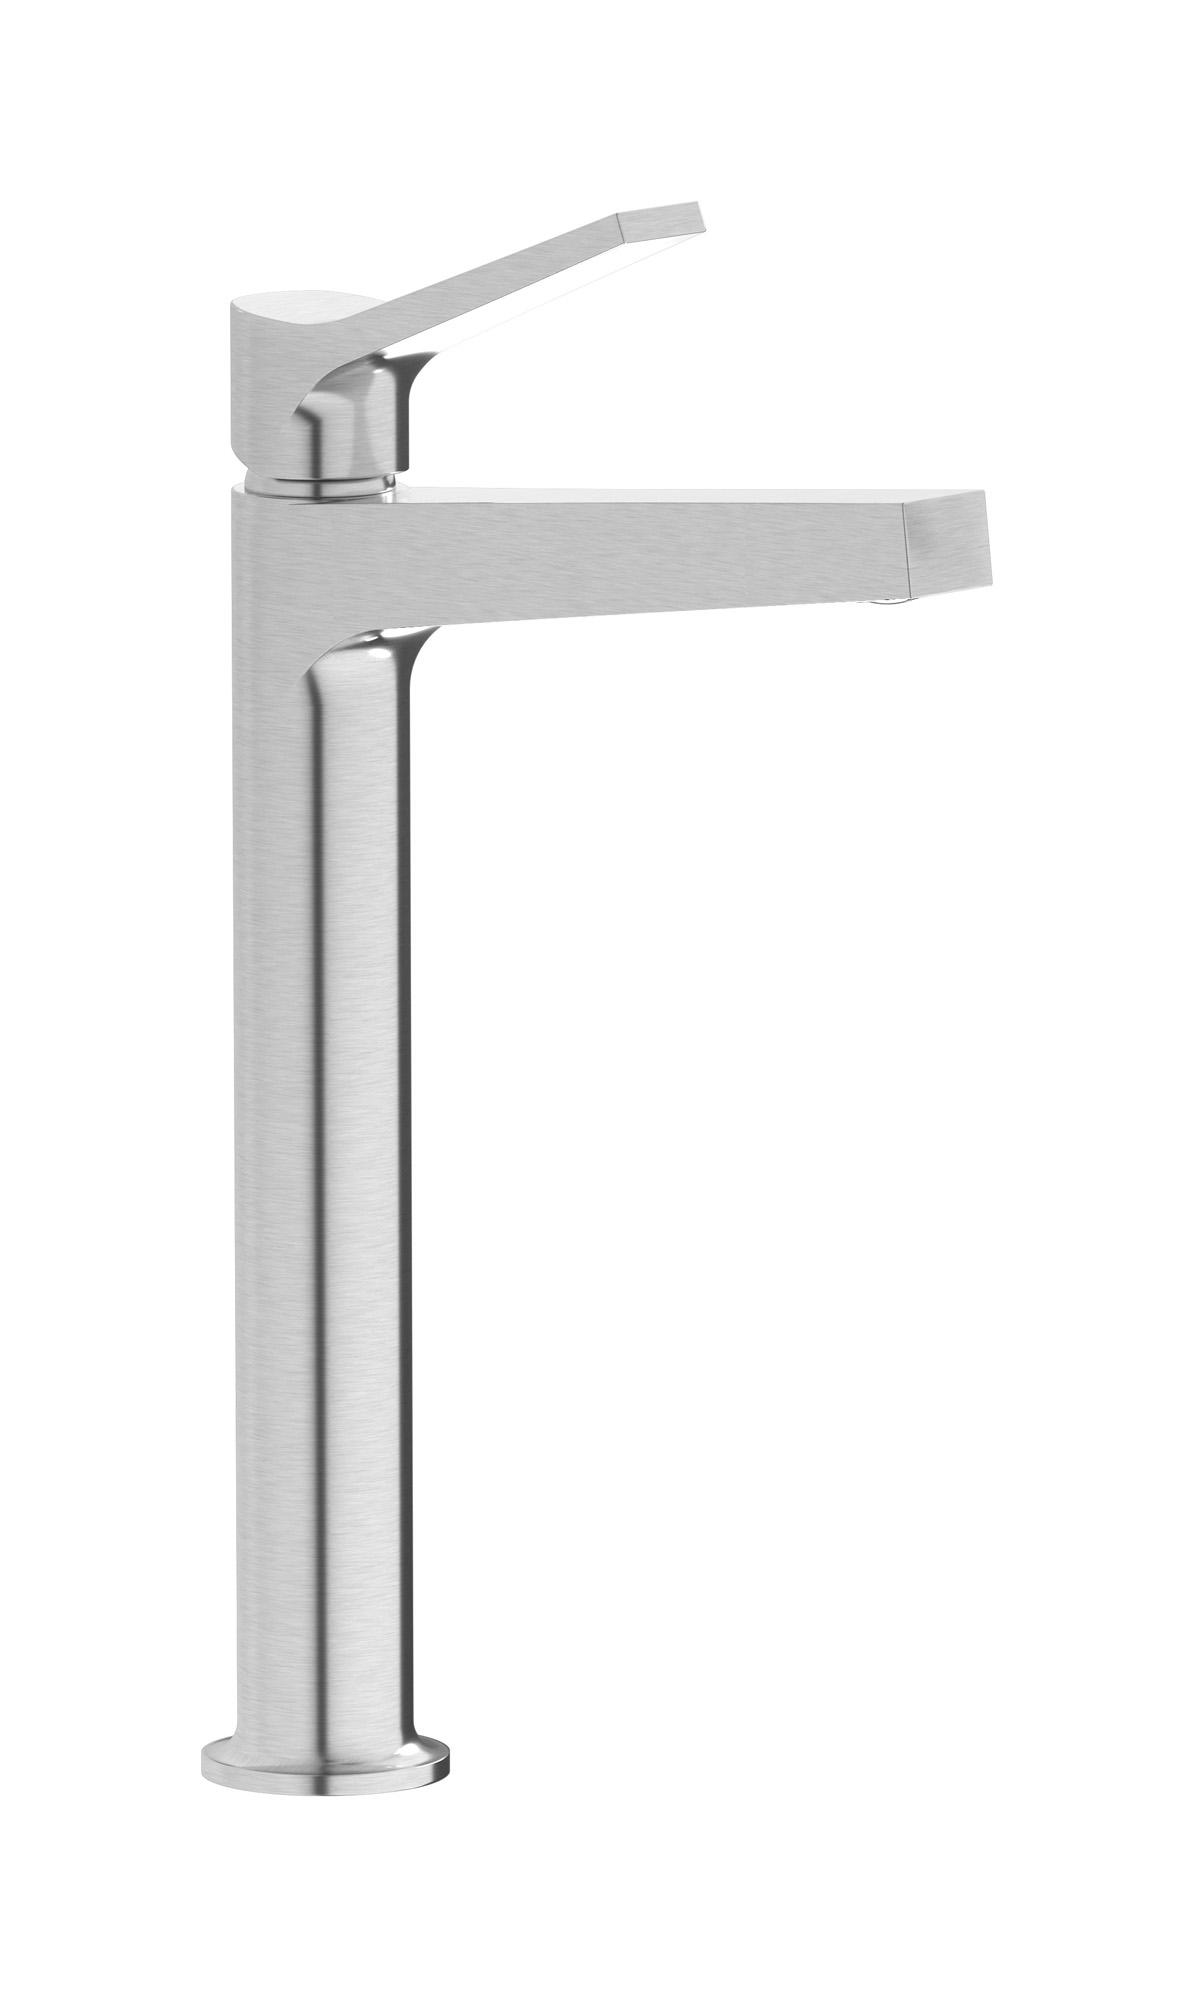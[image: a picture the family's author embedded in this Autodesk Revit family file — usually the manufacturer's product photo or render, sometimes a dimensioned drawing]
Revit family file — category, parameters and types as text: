
# Revit family: TW202
name_source: partatom
category: Apparecchi idraulici
units: mm (PartAtom-declared; Revit-internal decimal feet)

## family parameters
Basato su piano di lavoro = No
Condiviso = No
Mantieni orientamento annotazione = No
Numero OmniClass = 23.45.55.17
Punto di calcolo locali = No
Quota connettore circolare = Usa diametro
Sempre verticale = Sì
Taglio con vuoti quando caricato = No
Tipo di parte = Normale
Titolo OmniClass = Mixing Faucets

## types (12) — shared parameters
Cold water inlet = 10 mm  [stored 0.0328084 ft]
Commenti sul tipo = Washbasin mixer
Connessione CW = No
Connessione HW = No
Connessione di scarico = No
Connessione di ventilazione = No
Descrizione = Tall monohole washbasin mixer complete with drain
Hot water inlet = 10 mm  [stored 0.0328084 ft]
Produttore = IB Rubinetterie S.p.A.
URL = https://www.weareib.it
zero-valued in all types: Prospetto di default

## per-type parameters (varying)
| type | Finishes surface | Immagine tipo | Modello |
| Chrome | IB_Chrome | TW202CC.jpg | TW202CC |
| Brushed nickel | IB_Brushed nickel | TW202SS.jpg | TW202SS |
| Matt black | IB_matt black | TW202NP.jpg | TW202NP |
| Matt white | IB_matt white | TW202BO.jpg | TW202BO |
| Black chrome | IB_Black chrome | TW202CF.jpg | TW202CF |
| Brushed black chrome | IB_Brushed black chrome | TW202CS.jpg | TW202CS |
| Pale gold | IB_Pale gold | TW202II.jpg | TW202II |
| Brushed pale gold | IB_brushed pale gold | TW202IS.jpg | TW202IS |
| Rose gold | IB_Rose gold | TW202RS.jpg | TW202RS |
| Brushed rose gold | IB_Brushed rose gold | TW202SR.jpg | TW202SR |
| Gold | IB_gold | TW202OO.jpg | TW202OO |
| Brushed gold | IB_brushed gold | TW202OS.jpg | TW202OS |

note: [stored X ft] marks values corroborated as IEEE doubles in the binary element streams (Revit-internal decimal feet)
